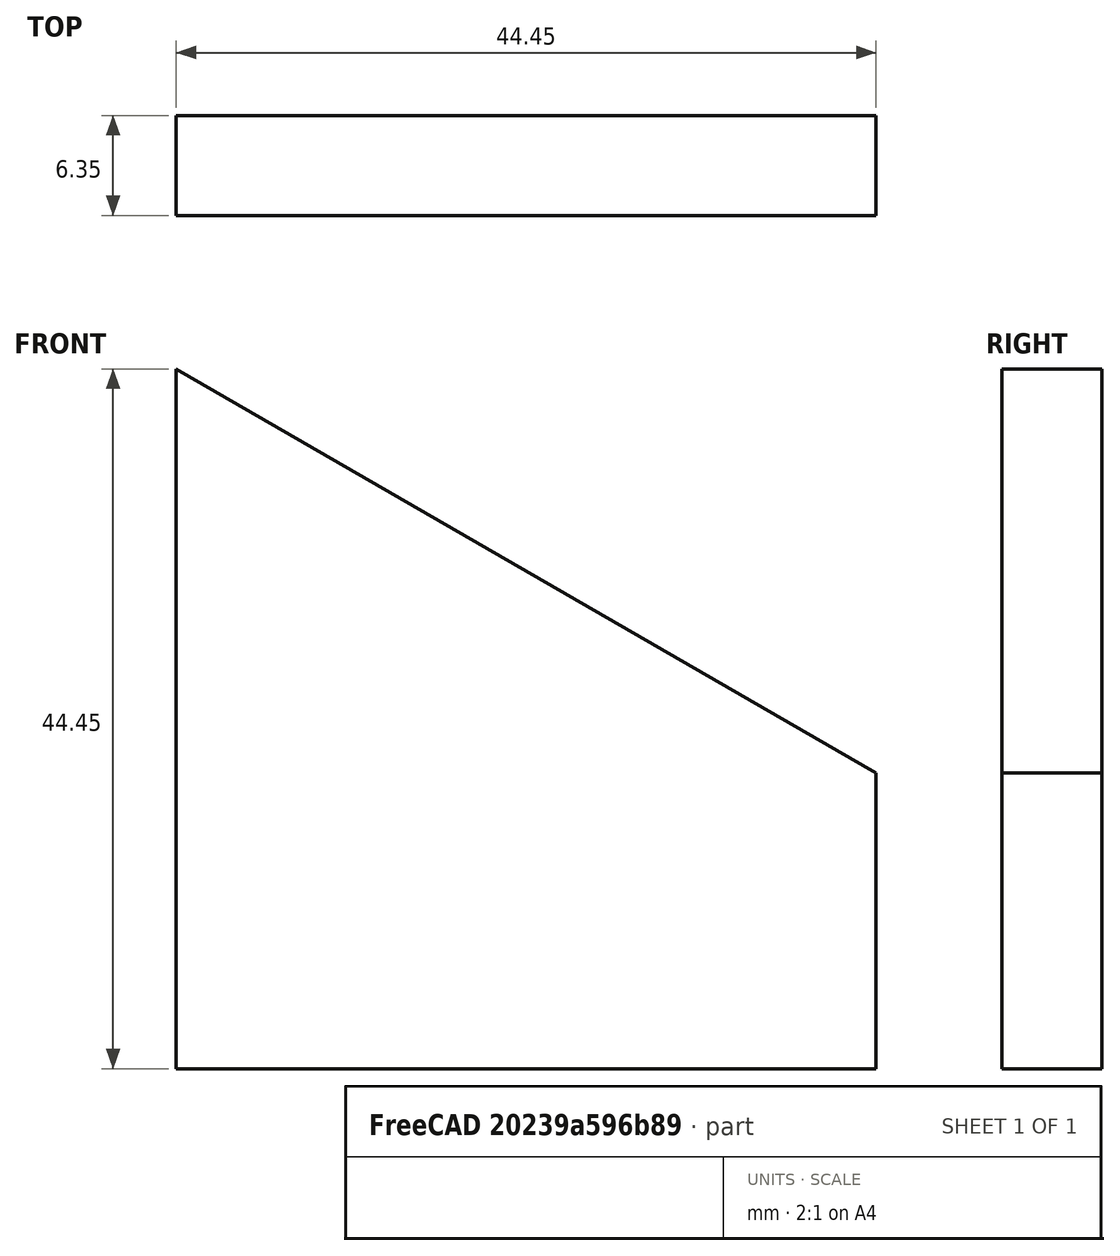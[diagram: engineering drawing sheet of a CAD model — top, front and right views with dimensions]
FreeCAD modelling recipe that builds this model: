
FCSTD DOCUMENT  (FreeCAD 0.17R13522 (Git))
Label: ssqa bottom brace
License: CreativeCommons Attribution-NonCommercial-ShareAlike
LicenseURL: http://creativecommons.org/licenses/by-nc-sa/4.0/
objects: Sketcher::SketchObject×1, PartDesign::Pad×1, PartDesign::Body×1
note: 4 computed .brp shape members not serialized (recipe doc carries the construction recipe); baked Part::Feature solids carry a one-line shape summary decoded from their .brp

FEATURE [Sketcher::SketchObject] Sketch
  MapMode = 5
  Placement = pos=(0,0,0) rot=(1,0,0;1.5708rad)
  Support = -> [XZ_Plane]
  sketch-geometry (4):
    g0: LineSegment StartX=0 StartY=0 StartZ=0 EndX=44.45 EndY=0 EndZ=0
    g1: LineSegment StartX=44.45 StartY=18.7868 StartZ=0 EndX=0 EndY=44.45 EndZ=0
    g2: LineSegment StartX=0 StartY=44.45 StartZ=0 EndX=0 EndY=0 EndZ=0
    g3: LineSegment StartX=44.45 StartY=0 StartZ=0 EndX=44.45 EndY=18.7868 EndZ=0
  constraints (11):
    c: Coincident(g-1,g0)
    c: Horizontal(g0)
    c: Coincident(g1,g2)
    c: Coincident(g2,g0)
    c: Vertical(g2)
    c: DistanceX(g0,g0) = 44.45
    c: DistanceY(g2,g2) = 44.45
    c: Vertical(g3)
    c: Coincident(g3,g1)
    c: Coincident(g3,g0)
    c: Angle(g1,g0) = 0.523599
FEATURE [PartDesign::Pad] Pad
  Length = 6.35
  Length2 = 99.9998
  Placement = pos=(0,0,0) rot=(1,0,0;1.5708rad)
  Profile = -> Sketch
  Type = 0
FEATURE [PartDesign::Body] Body
  Group = -> [Sketch,Pad]
  Origin = -> Origin
  Tip = -> Pad
